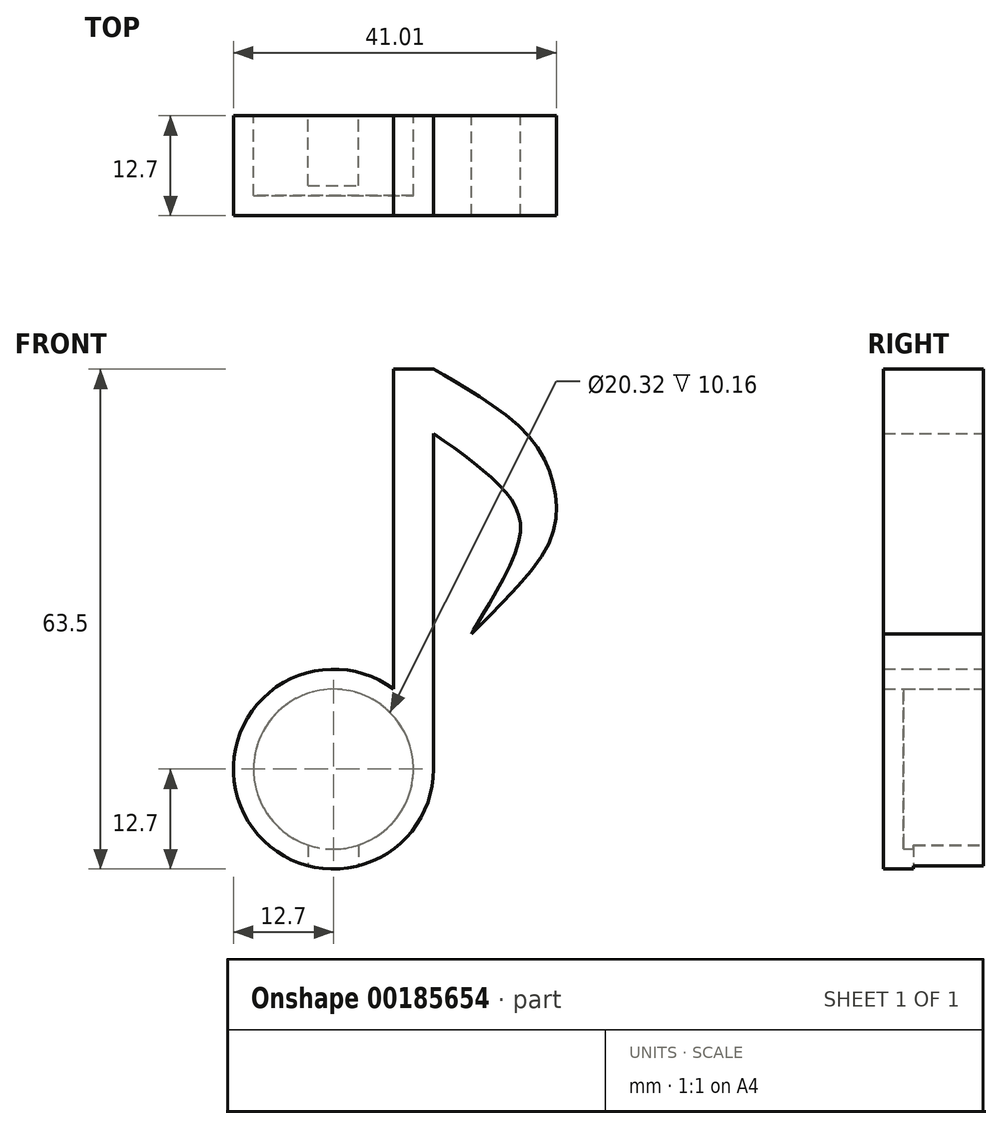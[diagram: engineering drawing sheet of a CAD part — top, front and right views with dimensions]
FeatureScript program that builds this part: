
annotation { "Feature Type Name" : "Feature", "Feature Type Description" : "" }
export const myFeature = defineFeature(function(context is Context, id is Id, definition is map)
    precondition{}
    {
        {
            var Q0;
            Q0=qCreatedBy(makeId("Front.planeOp"),FACE);
            var sketch = newSketch(context, id + "F0", { "sketchPlane" : qUnion([Q0])});
            skCircle(sketch, "E0", {"center": v(0, 0) * mm, "radius": 12.7 * mm});
            skLineSegment(sketch, "E1.bottom", {"start": v(12.7, 0) * mm, "end": v(7.62, 0) * mm});
            skLineSegment(sketch, "E1.top", {"start": v(12.7, 50.8) * mm, "end": v(7.62, 50.8) * mm});
            skLineSegment(sketch, "E1.left", {"start": v(12.7, 0) * mm, "end": v(12.7, 50.8) * mm});
            skLineSegment(sketch, "E1.right", {"start": v(7.62, 0) * mm, "end": v(7.62, 50.8) * mm});
            skCircle(sketch, "E2", {"center": v(0, 0) * mm, "radius": 10.16 * mm});
            skFitSpline(sketch, "E3", {"points": [v(12.7, 42.64) * mm, v(22.16, 34.83) * mm, v(23.22, 27.85) * mm, v(17.54, 17.2) * mm, v(17.54, 17.08) * mm], "startDerivative": vector(31.76, -22.32) * mm, "endDerivative": vector(1.09, -1.96) * mm});
            skFitSpline(sketch, "E4", {"points": [v(17.54, 17.2) * mm, v(26.77, 27.61) * mm, v(28.31, 32.94) * mm, v(27.48, 37.67) * mm, v(24.29, 42.88) * mm, v(17.54, 47.97) * mm, v(12.7, 50.8) * mm], "startDerivative": vector(47.86, 47.34) * mm, "endDerivative": vector(-30.75, 17.38) * mm});
            skSolve(sketch);
        }
        {
            var Q0;
            {var subQ1=sQuery(id+"F0.wireOp",EDGE,"E0");var subQ3=sQuery(id+"F0.wireOp",EDGE,"E1.right");var subQ4=makeQuery(id+"F0.imprint","INTERSECT",VERTEX,{"derivedFrom":[subQ1,subQ3]});Q0=makeQuery(id+"F0.imprint","IMPRINT",FACE,{"disambiguationData":[TD([[makeQuery(id+"F0.imprint","IMPRINT",EDGE,{"disambiguationData":[TD([[subQ4,1.0]])],"derivedFrom":subQ3}),1.0]])]});}
            var Q1;
            {var subQ1=sQuery(id+"F0.wireOp",EDGE,"E0");var subQ3=sQuery(id+"F0.wireOp",EDGE,"E1.right");var subQ4=makeQuery(id+"F0.imprint","INTERSECT",VERTEX,{"derivedFrom":[subQ1,subQ3]});Q1=makeQuery(id+"F0.imprint","IMPRINT",FACE,{"disambiguationData":[TD([[makeQuery(id+"F0.imprint","IMPRINT",EDGE,{"disambiguationData":[TD([[subQ4,1.0]])],"derivedFrom":subQ3}),-1.0]])]});}
            extrude(context, id + "F1", {"entities" : qUnion([Q0, Q1]), "depth" : 10.16 * mm});
        }
        {
            var Q0;
            {var subQ0=sQuery(id+"F0.wireOp",EDGE,"E1.right");var subQ1=sQuery(id+"F0.wireOp",EDGE,"E1.bottom");var subQ2=makeQuery(id+"F0.imprint","INTERSECT",VERTEX,{"derivedFrom":[subQ1,subQ0]});Q0=makeQuery(id+"F0.imprint","IMPRINT",FACE,{"disambiguationData":[TD([[makeQuery(id+"F0.imprint","IMPRINT",EDGE,{"disambiguationData":[TD([[subQ2,1.0]])],"derivedFrom":subQ1}),1.0]])]});}
            cPlane(context, id + "F2", {"entities" : qUnion([Q0]), "cplaneType" : CPlaneType.OFFSET, "offset" : 10.16 * mm, "width" : 152.4 * mm, "height" : 152.4 * mm});
        }
        {
            var Q0;
            Q0=qCreatedBy(id+"F2.planeOp",FACE);
            var sketch = newSketch(context, id + "F3", { "sketchPlane" : qUnion([Q0])});
            skCircle(sketch, "E5", {"center": v(0, 0) * mm, "radius": 12.7 * mm});
            skSolve(sketch);
        }
        {
            var Q0;
            Q0=makeQuery(id+"F3.imprint","IMPRINT",FACE,{"disambiguationData":[TD([[makeQuery(id+"F3.imprint","IMPRINT",EDGE,{"derivedFrom":sQuery(id+"F3.wireOp",EDGE,"E5")}),1.0]])]});
            extrude(context, id + "F4", {"entities" : qUnion([Q0]), "operationType" : NewBodyOperationType.ADD, "depth" : 2.54 * mm});
        }
        {
            var Q0;
            {var subQ1=sQuery(id+"F0.wireOp",EDGE,"E1.top");Q0=makeQuery(id+"F0.imprint","IMPRINT",FACE,{"disambiguationData":[TD([[makeQuery(id+"F0.imprint","IMPRINT",EDGE,{"derivedFrom":subQ1}),1.0]])]});}
            var Q1;
            {var subQ0=sQuery(id+"F0.wireOp",EDGE,"E4");Q1=makeQuery(id+"F0.imprint","IMPRINT",FACE,{"disambiguationData":[TD([[makeQuery(id+"F0.imprint","IMPRINT",EDGE,{"derivedFrom":subQ0}),1.0]])]});}
            var Q2;
            Q2 = qSketchRegion(id + "F6", true);
            extrude(context, id + "F5", {"entities" : qUnion([Q0, Q1, Q2]), "operationType" : NewBodyOperationType.ADD, "depth" : 12.7 * mm});
        }
        {
            var Q0;
            Q0=qCreatedBy(makeId("Front.planeOp"),FACE);
            var sketch = newSketch(context, id + "F6", { "sketchPlane" : qUnion([Q0])});
            skLineSegment(sketch, "E6.bottom", {"start": v(3.16, -9.46) * mm, "end": v(-3.24, -9.46) * mm});
            skLineSegment(sketch, "E6.top", {"start": v(3.16, -14.19) * mm, "end": v(-3.24, -14.19) * mm});
            skLineSegment(sketch, "E6.left", {"start": v(3.16, -9.46) * mm, "end": v(3.16, -14.19) * mm});
            skLineSegment(sketch, "E6.right", {"start": v(-3.24, -9.46) * mm, "end": v(-3.24, -14.19) * mm});
            skSolve(sketch);
        }
        {
            var Q0;
            Q0 = qSketchRegion(id + "F6", true);
            extrude(context, id + "F7", {"entities" : qUnion([Q0]), "operationType" : NewBodyOperationType.REMOVE, "depth" : 8.9 * mm});
        }
    });
